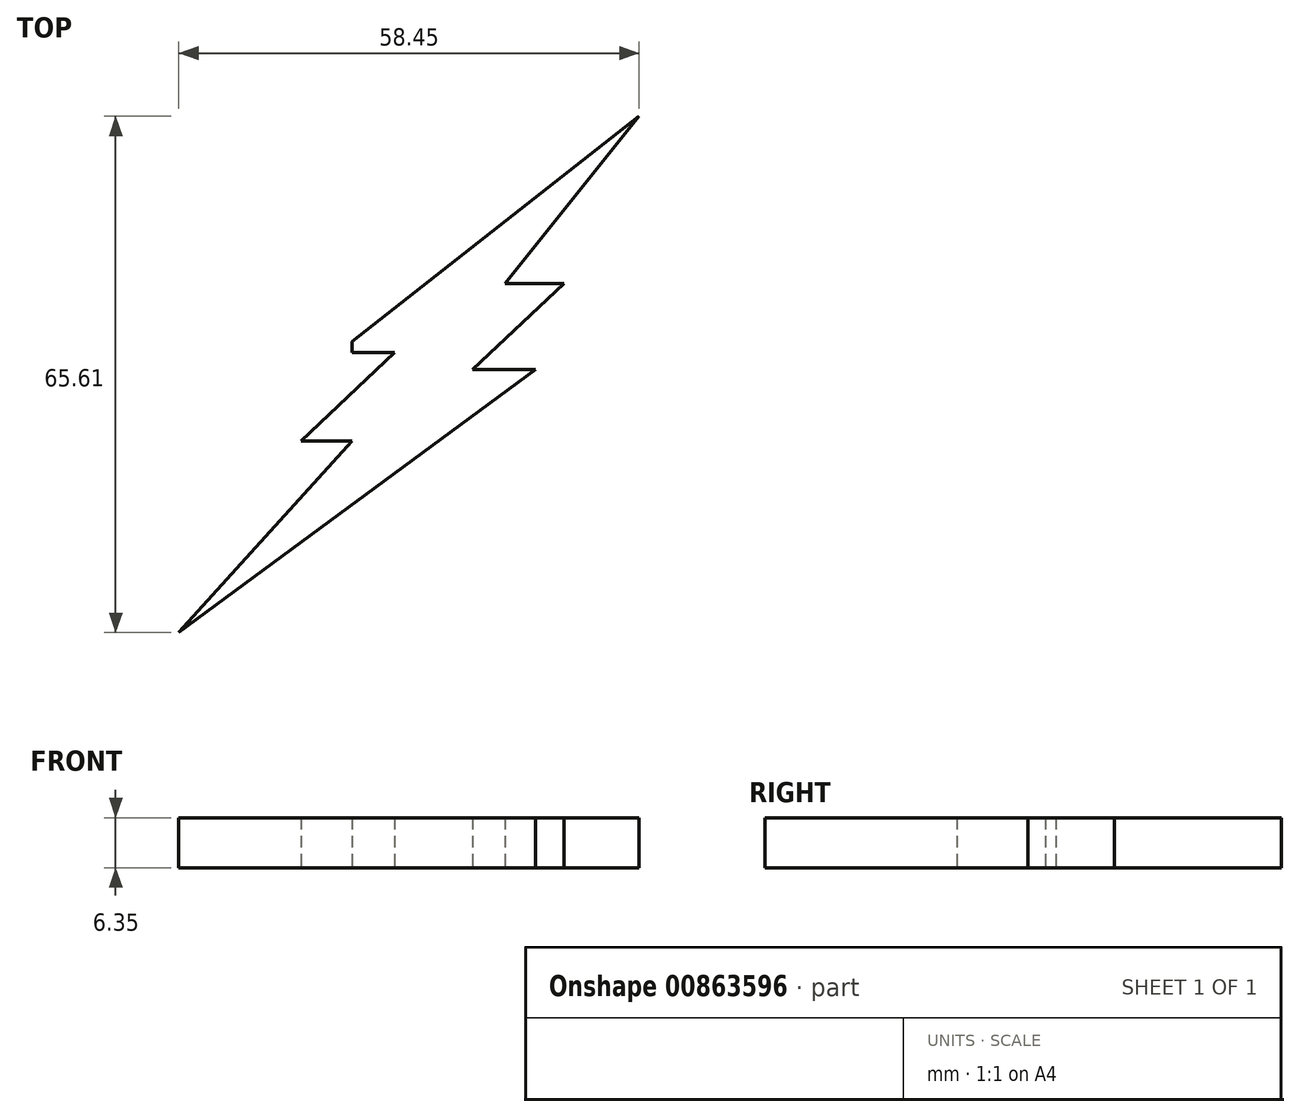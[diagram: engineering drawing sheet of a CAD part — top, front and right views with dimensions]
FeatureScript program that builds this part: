
annotation { "Feature Type Name" : "Feature", "Feature Type Description" : "" }
export const myFeature = defineFeature(function(context is Context, id is Id, definition is map)
    precondition{}
    {
        {
            var Q0;
            Q0=qCreatedBy(makeId("Top.planeOp"),FACE);
            var sketch = newSketch(context, id + "F0", { "sketchPlane" : qUnion([Q0])});
            skLineSegment(sketch, "E0", {"start": v(-2.91, 39.88) * mm, "end": v(-14.84, 28.63) * mm});
            skLineSegment(sketch, "E1", {"start": v(-8.36, 28.63) * mm, "end": v(-16.37, 28.63) * mm});
            skLineSegment(sketch, "E2", {"start": v(-8.36, 28.63) * mm, "end": v(-30.35, 4.26) * mm});
            skLineSegment(sketch, "E3", {"start": v(-30.35, 4.26) * mm, "end": v(14.98, 37.66) * mm});
            skLineSegment(sketch, "E4", {"start": v(14.98, 37.66) * mm, "end": v(6.97, 37.66) * mm});
            skLineSegment(sketch, "E5", {"start": v(6.97, 37.66) * mm, "end": v(18.61, 48.63) * mm});
            skLineSegment(sketch, "E6", {"start": v(18.61, 48.63) * mm, "end": v(11.06, 48.63) * mm});
            skLineSegment(sketch, "E7", {"start": v(11.06, 48.63) * mm, "end": v(28.1, 69.87) * mm});
            skLineSegment(sketch, "E8", {"start": v(28.1, 69.87) * mm, "end": v(-8.36, 41.24) * mm});
            skLineSegment(sketch, "E9", {"start": v(-2.91, 39.88) * mm, "end": v(-8.36, 39.88) * mm});
            skLineSegment(sketch, "E10", {"start": v(-8.36, 39.88) * mm, "end": v(-8.36, 41.24) * mm});
            skLineSegment(sketch, "E11", {"start": v(-8.36, 41.24) * mm, "end": v(-8.36, 39.88) * mm});
            skSolve(sketch);
        }
        {
            var Q0;
            Q0 = qSketchRegion(id + "F0", true);
            extrude(context, id + "F1", {"entities" : qUnion([Q0]), "depth" : 6.35 * mm, "offsetDistance" : 25.4 * mm});
        }
    });
